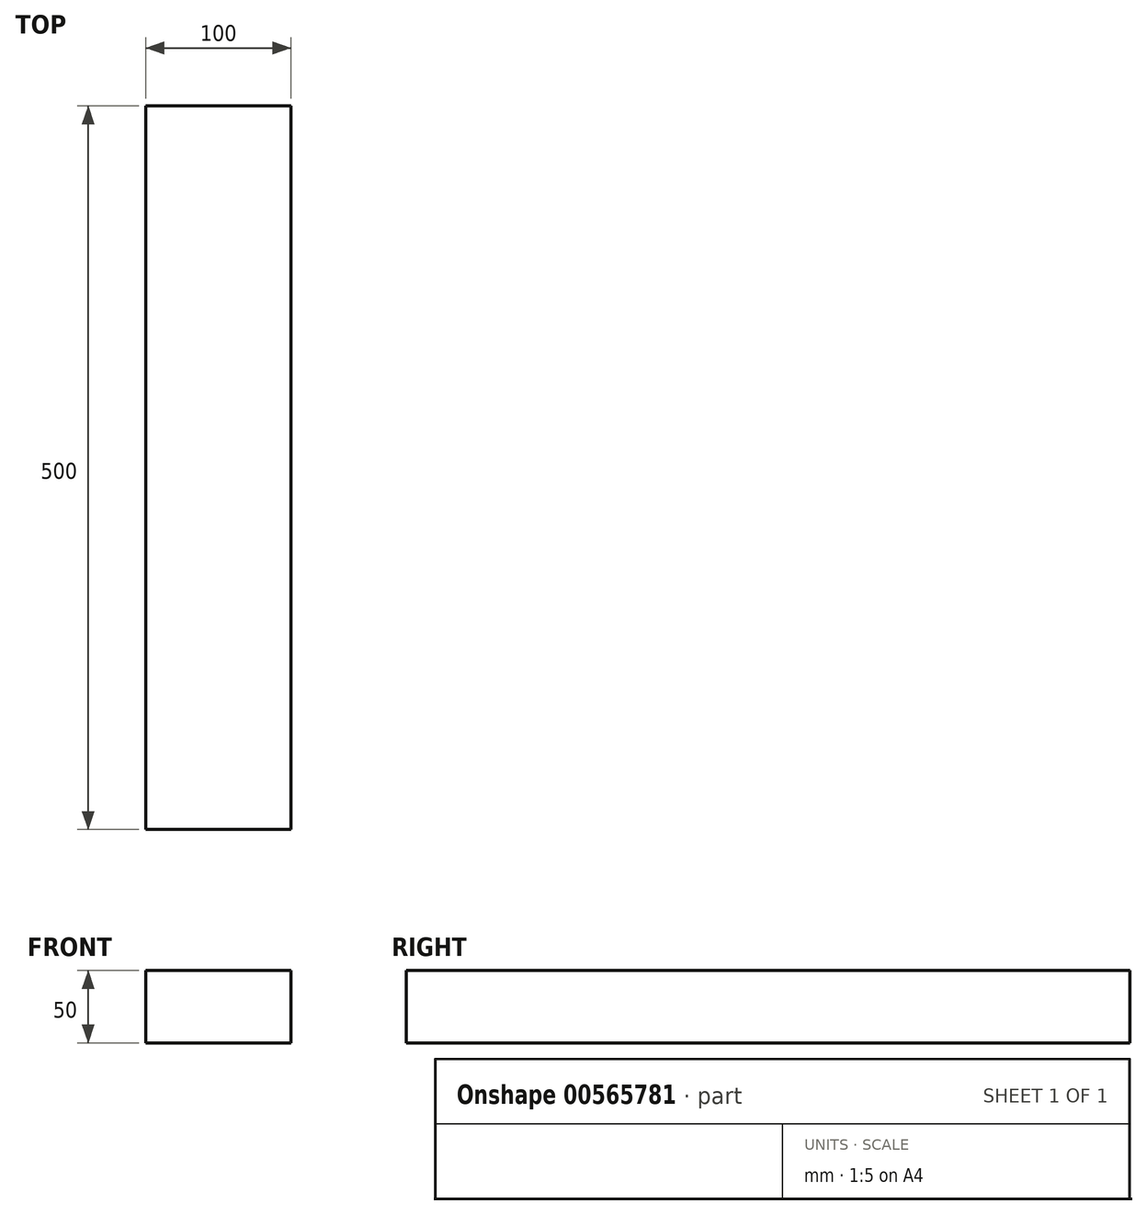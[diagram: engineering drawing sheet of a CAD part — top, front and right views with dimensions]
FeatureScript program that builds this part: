
annotation { "Feature Type Name" : "Feature", "Feature Type Description" : "" }
export const myFeature = defineFeature(function(context is Context, id is Id, definition is map)
    precondition{}
    {
        {
            var Q0;
            Q0=qCreatedBy(makeId("Front.planeOp"),FACE);
            var sketch = newSketch(context, id + "F0", { "sketchPlane" : qUnion([Q0])});
            skLineSegment(sketch, "E0.bottom", {"start": v(50, -25) * mm, "end": v(-50, -25) * mm});
            skLineSegment(sketch, "E0.top", {"start": v(50, 25) * mm, "end": v(-50, 25) * mm});
            skLineSegment(sketch, "E0.left", {"start": v(50, -25) * mm, "end": v(50, 25) * mm});
            skLineSegment(sketch, "E0.right", {"start": v(-50, -25) * mm, "end": v(-50, 25) * mm});
            skPoint(sketch, "E0.middle", {"position": v(0, 0) * mm});
            skSolve(sketch);
        }
        {
            var Q0;
            Q0 = qSketchRegion(id + "F0", true);
            extrude(context, id + "F1", {"entities" : qUnion([Q0]), "depth" : 500 * mm, "offsetDistance" : 25 * mm});
        }
    });
